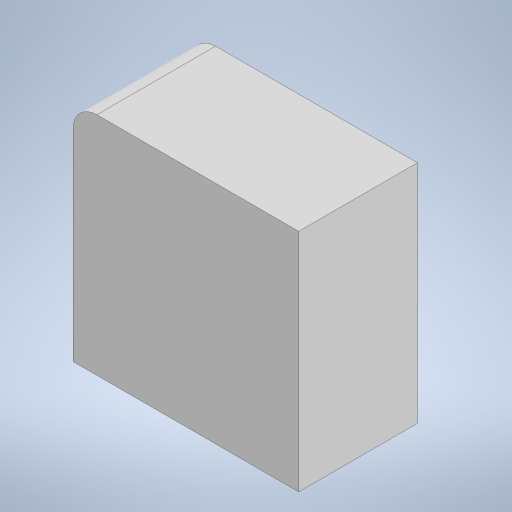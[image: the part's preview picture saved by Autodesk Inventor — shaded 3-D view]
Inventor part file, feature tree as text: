
AUTODESK INVENTOR PART (.ipt)
format: ipt  version: 2023 (Build 270158000, 158)  size: 193,536 bytes
history: native  units: mm
features: extrude x2, sketch x2, fillet x1
ambient origin geometry x8: Origin, YZ Plane, XZ Plane, XY Plane, X Axis, Y Axis, Z Axis, Center Point
bodies: Solide1 (feature_tree)
feature tree (5):
  extrude  "Extrusion1"  Depth=9.0mm
  extrude  "Extrusion2"  Depth=9.0mm
  fillet  "Congé1"  Radius=1.8mm
  sketch  "Esquisse1"
  sketch  "Esquisse2"
